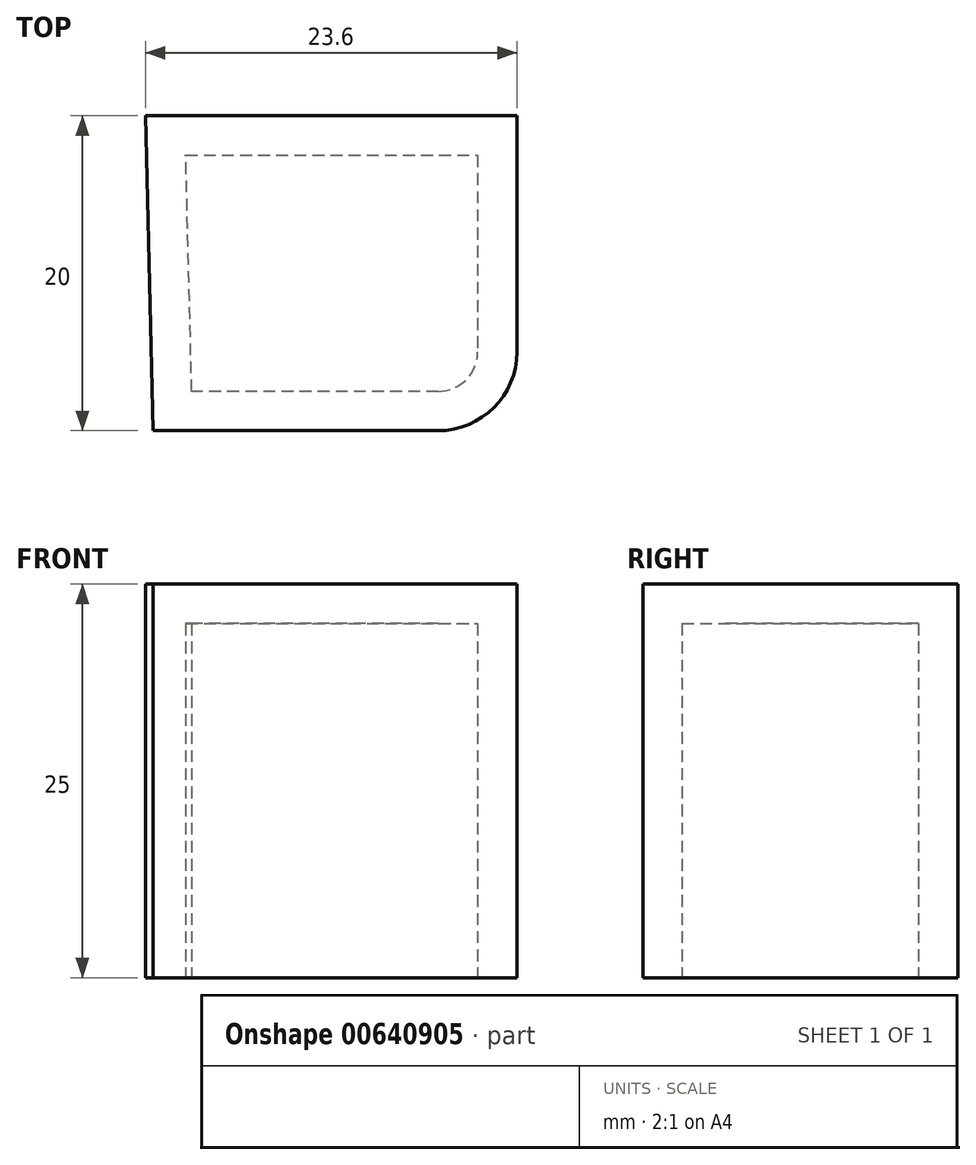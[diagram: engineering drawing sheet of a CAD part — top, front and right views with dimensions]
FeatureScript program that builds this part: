
annotation { "Feature Type Name" : "Feature", "Feature Type Description" : "" }
export const myFeature = defineFeature(function(context is Context, id is Id, definition is map)
    precondition{}
    {
        {
            var Q0;
            Q0=qCreatedBy(makeId("Top.planeOp"),FACE);
            var sketch = newSketch(context, id + "F0", { "sketchPlane" : qUnion([Q0])});
            skLineSegment(sketch, "E0", {"start": v(-63.1, 47.42) * mm, "end": v(-39.5, 47.42) * mm});
            skLineSegment(sketch, "E1", {"start": v(-39.5, 47.42) * mm, "end": v(-39.5, 27.42) * mm});
            skLineSegment(sketch, "E2", {"start": v(-39.5, 27.42) * mm, "end": v(-62.6, 27.42) * mm});
            skLineSegment(sketch, "E3", {"start": v(-62.6, 27.42) * mm, "end": v(-63.1, 47.42) * mm});
            skSolve(sketch);
        }
        {
            var Q0;
            Q0=makeQuery(id+"F0.imprint","IMPRINT",FACE,{"disambiguationData":[TD([[makeQuery(id+"F0.imprint","IMPRINT",EDGE,{"derivedFrom":sQuery(id+"F0.wireOp",EDGE,"E0")}),-1.0]])]});
            extrude(context, id + "F1", {"entities" : qUnion([Q0]), "depth" : 25 * mm, "offsetDistance" : 25 * mm});
        }
        {
            var Q0;
            Q0=makeQuery(id+"F1.opExtrude","SWEPT_EDGE",EDGE,{"disambiguationData":[OSD([sQuery(id+"F0.wireOp",EDGE,"E1"),sQuery(id+"F0.wireOp",EDGE,"E2")])]});
            fillet(context, id + "F2", {"entities" : qUnion([Q0]), "radius" : 5 * mm, "tangentPropagation" : true, "allowEdgeOverflow" : false});
        }
        {
            var Q0;
            Q0=makeQuery(id+"F1.opExtrude","CAP_FACE",FACE,{"disambiguationData":[OSD([sQuery(id+"F0.wireOp",EDGE,"E0"),sQuery(id+"F0.wireOp",EDGE,"E1"),sQuery(id+"F0.wireOp",EDGE,"E2"),sQuery(id+"F0.wireOp",EDGE,"E3")])],"isStart":true});
            shell(context, id + "F3", {"entities" : qUnion([Q0]), "thickness" : 2.5 * mm});
        }
    });
